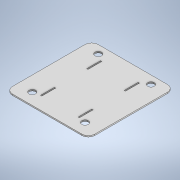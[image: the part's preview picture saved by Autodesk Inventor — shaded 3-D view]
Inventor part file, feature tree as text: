
AUTODESK INVENTOR PART (.ipt)
format: ipt  version: 2022 (Build 260153000, 153)  size: 165,376 bytes
history: native  units: mm
features: extrude x2, sketch x2, fillet x1, projected_geometry x1
ambient origin geometry x8: Origin, YZ Plane, XZ Plane, XY Plane, X Axis, Y Axis, Z Axis, Center Point
bodies: Solid1 (feature_tree)
feature tree (6):
  extrude  "Extrusion1"  Depth=125.0mm
  extrude  "Extrusion2"  Depth=10.0mm
  fillet  "Fillet1"  Radius=100.0mm
  sketch  "Sketch1"  dims[d0=130.0mm d1=125.0mm]
  sketch  "Sketch2"  dims[d2=10.0mm d3=10.0mm d4=100.0mm d5=10.0mm d6=10.0mm d7=100.0mm d8=80.0mm d9=80.0mm d10=17.5mm d11=22.5mm d12=17.5mm d13=22.5mm d14=2.0mm d15=0.0mm d16=55.0mm d17=100.0mm d18=125.0mm d19=35.0mm d20=2.0mm d21=2.0mm d22=2.0mm d23=2.0mm d24=21.0mm d25=21.0mm d26=21.0mm d27=21.0mm d28=19.5mm d29=19.5mm d30=19.5mm d31=19.5mm d32=0.0mm d33=0.0mm d34=10.0mm]
  projected_geometry  "Projected Loop1"
